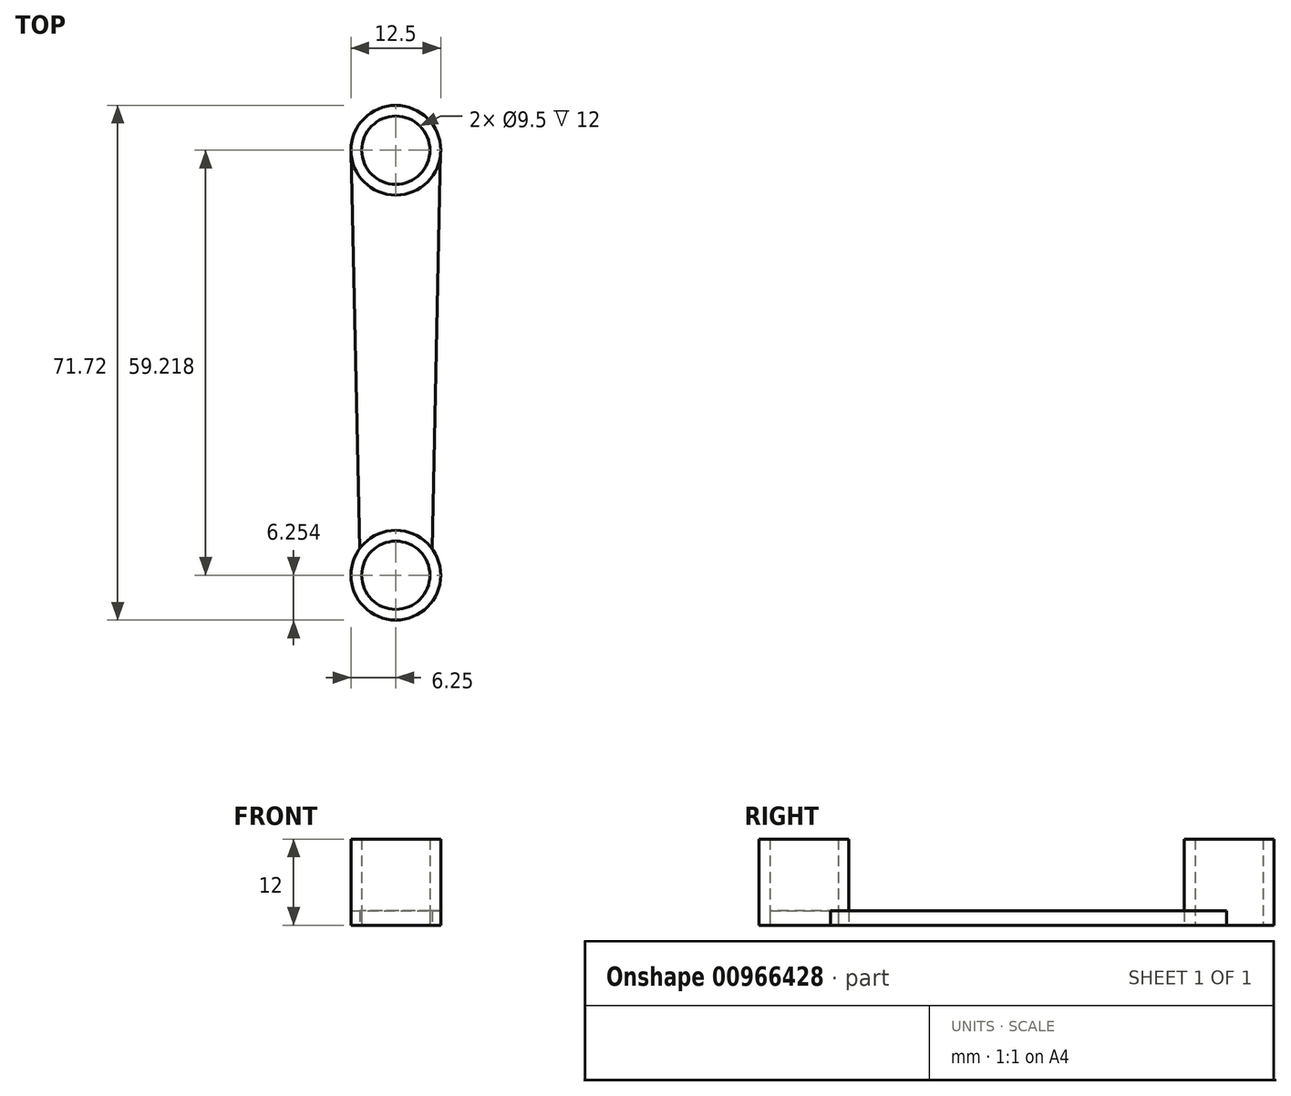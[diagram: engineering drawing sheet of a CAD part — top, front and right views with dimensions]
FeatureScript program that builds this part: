
annotation { "Feature Type Name" : "Feature", "Feature Type Description" : "" }
export const myFeature = defineFeature(function(context is Context, id is Id, definition is map)
    precondition{}
    {
        {
            var Q0;
            Q0=qCreatedBy(makeId("Top.planeOp"),FACE);
            var sketch = newSketch(context, id + "F0", { "sketchPlane" : qUnion([Q0])});
            skCircle(sketch, "E0", {"center": v(0, -36.3) * mm, "radius": 4.75 * mm});
            skCircle(sketch, "E1", {"center": v(0, -36.3) * mm, "radius": 6.25 * mm});
            skCircle(sketch, "E2", {"center": v(0, 22.91) * mm, "radius": 4.75 * mm});
            skCircle(sketch, "E3", {"center": v(0, 22.91) * mm, "radius": 6.25 * mm});
            skLineSegment(sketch, "E4", {"start": v(0, 16.66) * mm, "end": v(0, -30.06) * mm});
            skLineSegment(sketch, "E5", {"start": v(-6.24, 22.58) * mm, "end": v(-5.04, -32.62) * mm});
            skLineSegment(sketch, "E6.MirrorCS", {"start": v(6.24, 22.58) * mm, "end": v(5.04, -32.62) * mm});
            skSolve(sketch);
        }
        {
            var Q0;
            {var subQ0=sQuery(id+"F0.wireOp",EDGE,"E4");Q0=makeQuery(id+"F0.imprint","IMPRINT",FACE,{"disambiguationData":[TD([[makeQuery(id+"F0.imprint","IMPRINT",EDGE,{"derivedFrom":subQ0}),-1.0]])]});}
            var Q1;
            Q1=makeQuery(id+"F0.imprint","IMPRINT",FACE,{"disambiguationData":[TD([[makeQuery(id+"F0.imprint","IMPRINT",EDGE,{"derivedFrom":sQuery(id+"F0.wireOp",EDGE,"E0")}),1.0]])]});
            var Q2;
            {var subQ0=sQuery(id+"F0.wireOp",EDGE,"E4");Q2=makeQuery(id+"F0.imprint","IMPRINT",FACE,{"disambiguationData":[TD([[makeQuery(id+"F0.imprint","IMPRINT",EDGE,{"derivedFrom":subQ0}),1.0]])]});}
            extrude(context, id + "F1", {"entities" : qUnion([Q0, Q1, Q2]), "depth" : 2 * mm, "offsetDistance" : 25 * mm});
        }
        {
            var Q0;
            Q0=makeQuery(id+"F0.imprint","IMPRINT",FACE,{"disambiguationData":[TD([[makeQuery(id+"F0.imprint","IMPRINT",EDGE,{"derivedFrom":sQuery(id+"F0.wireOp",EDGE,"E2")}),-1.0]])]});
            var Q1;
            Q1=makeQuery(id+"F0.imprint","IMPRINT",FACE,{"disambiguationData":[TD([[makeQuery(id+"F0.imprint","IMPRINT",EDGE,{"derivedFrom":sQuery(id+"F0.wireOp",EDGE,"E0")}),-1.0]])]});
            extrude(context, id + "F2", {"entities" : qUnion([Q0, Q1]), "depth" : 12 * mm, "offsetDistance" : 25 * mm});
        }
    });
